# Revit family: LEGRAND_INTERLOCKED SOCKETS_FLUSH MOUNTED_230
name_source: partatom
category: Installations électriques
revit_build: Autodesk Revit 2018 (Build: 20170223_1515(x64)
units: mm (PartAtom-declared; Revit-internal decimal feet)

## family parameters
Conserver l'orientation des annotations = Non
Cote de connecteur circulaire = Utiliser le diamètre
Couper avec des vides une fois chargée = Non
Hôte = Face
Partagée = Non
Point de calcul de pièce = Non
Type d'élément = Normal

## types (10) — shared parameters
Description = Inter-locked socket at International Standard for flush or surface mounting with accessory allows connection and disconnection out of load for security of machines and persons.
Elévation par défaut = 1000 mm  [stored 3.28084 ft]
Fabricant = Legrand
Flush E or Surface mounting S = flush and surface mounting
General Conditions of Use = https://export.legrand.com
Maximum installation temperature = 40°C
Maximum use temperature = 100°C
Minimum installation temperature = -20°C
Minimum use temperature = -20°C
Standard IEC or NFC = IEC
Tension V = 230 V  50/60 Hz blue
characteristic color = blue
interlocking type = electrical and mechanical locking
protection class IP = IP55

## per-type parameters (varying)
| type | A1 | Modèle | Number of poles | Position of earth h | depth for flush mounting mm | depth mm | halogen free | height mm | horizontal fixing distance mm | intensity A | material of box | resistance to chocks IK | vertical fixing distance mm | width mm |
| Panel mounting socket Prisinter Hypra  IP44/55  16 A   200/250 V  2P+E  métal | Non | 052012 | 3 | 6 | 46 mm | 116 mm | Oui | 115 mm | 100 mm  [stored 0.328084 ft] | 16 A | metal | 10 | 100 mm  [stored 0.328084 ft] | 115 mm |
| Panel mounting socket Prisinter Hypra   IP44/55  16 A  200/250 V  2P+E  plastic | Non | 052002 | 3 | 6 | 46 mm | 116 mm | Non | 115 mm | 100 mm  [stored 0.328084 ft] | 16 A | plastic | 09 | 100 mm  [stored 0.328084 ft] | 115 mm |
| Panel mounting socket Prisinter Hypra  IP44/55  16 A  200/250 V 3P+N+E  plastic | Non | 052004 | 5 | 9 | 46 mm | 121 mm | Non | 125 mm | 110 mm | 16 A | plastic | 09 | 110 mm | 125 mm |
| Panel mounting socket Prisinter Hypra  IP44/55  16 A  200/250 V 3P+E  plast | Non | 052003 | 4 | 9 | 46 mm | 116 mm | Non | 115 mm | 100 mm  [stored 0.328084 ft] | 16 A | plastic | 09 | 100 mm  [stored 0.328084 ft] | 115 mm |
| Panel mounting socket Prisinter Hypra  IP44/55  32 A  200/250 V  2P+E  plast | Non | 052702 | 3 | 6 | 54 mm | 131 mm  [stored 0.42979 ft] | Non | 143 mm | 125 mm | 32 A | plastic | 09 | 125 mm | 143 mm |
| Panel mounting socket Prisinter Hypra  IP44/55  32 A  200/250 V 3P+E  métal | Non | 052713 | 4 | 9 | 54 mm | 131 mm  [stored 0.42979 ft] | Oui | 143 mm | 125 mm | 32 A | metal | 10 | 125 mm | 143 mm |
| Panel mounting socket Prisinter Hypra  IP44/55  32 A  200/250 V  3P+E  plast | Non | 052703 | 4 | 9 | 54 mm | 131 mm  [stored 0.42979 ft] | Non | 143 mm | 125 mm | 32 A | plastic | 09 | 125 mm | 143 mm |
| Panel mounting socket Prisinter Hypra  IP44/55  63 A  200/250 V  2P+E  métal | Oui | 053812 | 3 | 6 | 55 mm  [stored 0.180446 ft] | 154 mm  [stored 0.505249 ft] | Oui | 143 mm | 125 mm | 63 A | metal | 10 | 125 mm | 143 mm |
| Panel mounting socket Prisinter Hypra IP44/55 - 63 A - 200/250 V - 3P+E - plast | Oui | 053602 | 4 | 9 | 55 mm  [stored 0.180446 ft] | 154 mm  [stored 0.505249 ft] | Non | 143 mm | 125 mm | 63 A | plastic | 09 | 125 mm | 143 mm |
| Panel mounting socket Prisinter Hypra IP44/55  63 A  200/250 V  2P+E  plast | Oui | 053601 | 3 | 6 | 55 mm  [stored 0.180446 ft] | 154 mm  [stored 0.505249 ft] | Non | 143 mm | 125 mm | 63 A | plastic | 10 | 125 mm | 143 mm |

note: [stored X ft] marks values corroborated as IEEE doubles in the binary element streams (Revit-internal decimal feet)
